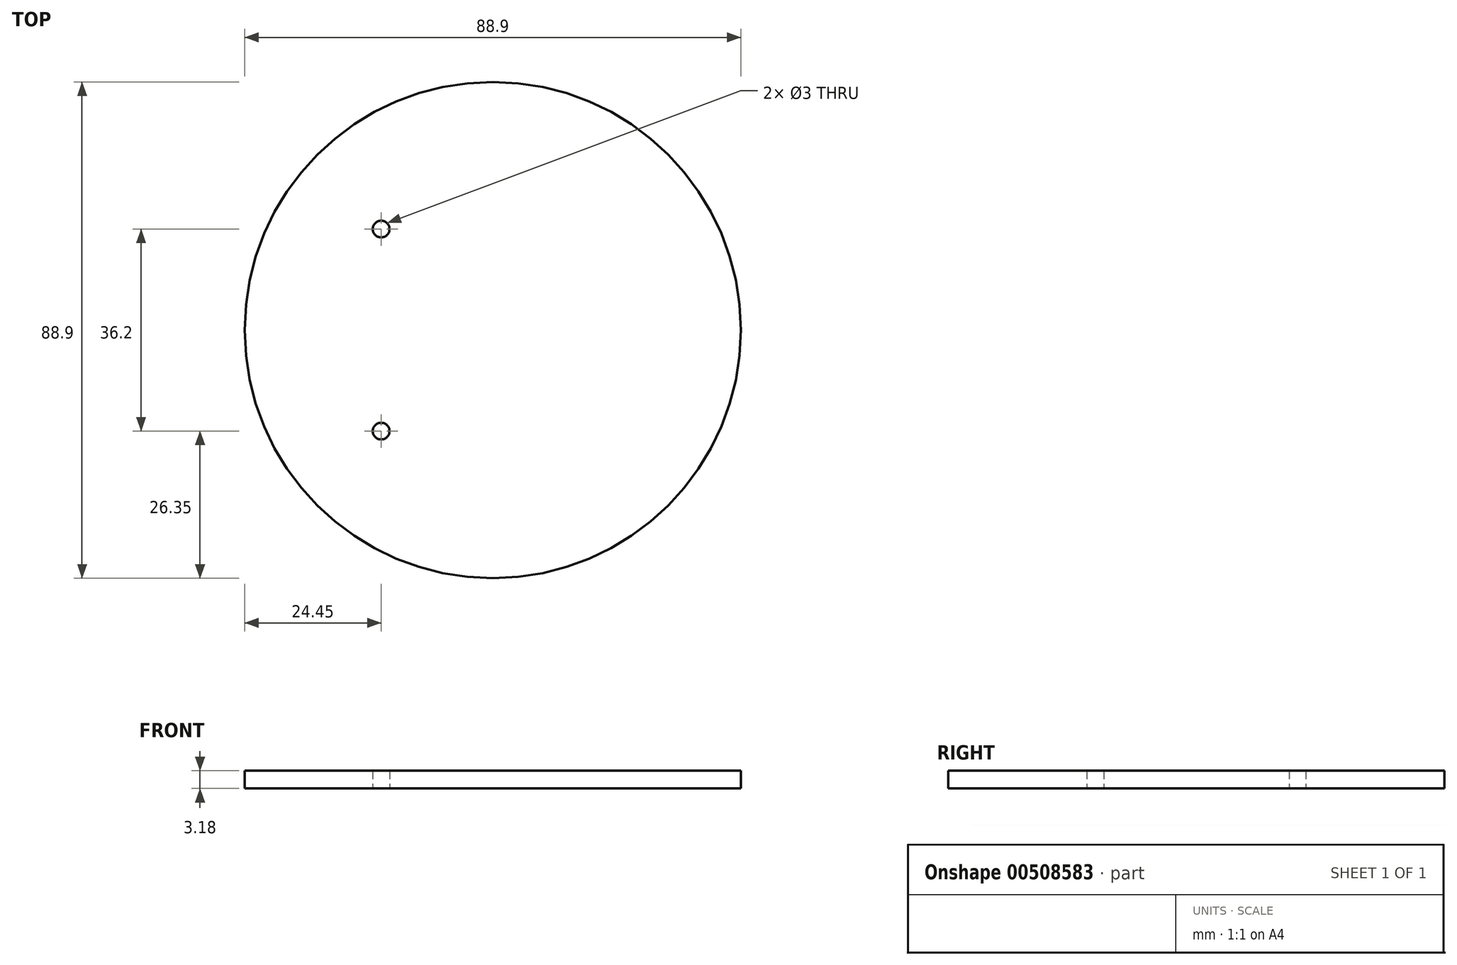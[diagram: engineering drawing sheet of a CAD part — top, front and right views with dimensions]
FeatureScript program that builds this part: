
annotation { "Feature Type Name" : "Feature", "Feature Type Description" : "" }
export const myFeature = defineFeature(function(context is Context, id is Id, definition is map)
    precondition{}
    {
        {
            var Q0;
            Q0=qCreatedBy(makeId("Top.planeOp"), FACE);
            var sketch = newSketch(context, id + "F0", { "sketchPlane" : qUnion([Q0])});
            skCircle(sketch, "E0", {"center": v(0, 0) * mm, "radius": 44.45 * mm});
            skLineSegment(sketch, "E1", {"start": v(0, 0) * mm, "end": v(0, 26.08) * mm, "construction": true});
            skCircle(sketch, "E2", {"center": v(-20, 18.1) * mm, "radius": 1.5 * mm});
            skCircle(sketch, "E3", {"center": v(-20, -18.1) * mm, "radius": 1.5 * mm});
            skLineSegment(sketch, "E4", {"start": v(-20, 18.1) * mm, "end": v(-20, 0) * mm, "construction": true});
            skLineSegment(sketch, "E5", {"start": v(-20, 0) * mm, "end": v(-20, -18.1) * mm, "construction": true});
            skSolve(sketch);
        }
        {
            var Q0;
            Q0 = qSketchRegion(id + "F0", true);
            extrude(context, id + "F1", {"entities" : qUnion([Q0]), "depth" : (25.4 / 8) * mm, "offsetDistance" : 25 * mm});
        }
    });
